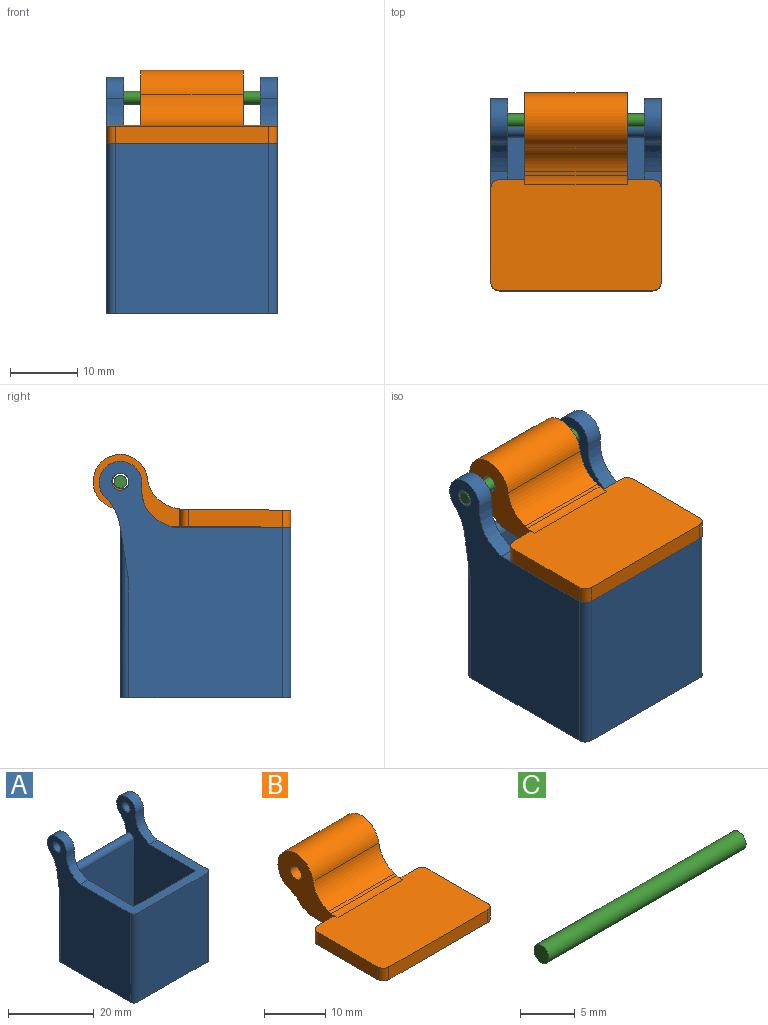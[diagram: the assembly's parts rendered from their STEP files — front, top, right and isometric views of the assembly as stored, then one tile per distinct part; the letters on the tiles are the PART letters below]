
ASSEMBLY  parts=3 mates=2
PART A: 24 faces, bbox 25.4x28.6x35.2 mm
  f0: plane 25.4x17.7mm, normal (0,0,1), area 140.8mm2, adj f1,f2,f4,f6,f9,f10,f13,f15
  f1: plane 35.19x27.31mm, normal (1,0,0), area 634.1mm2, adj f0,f3,f6,f7,f8,f18,f20,f23
  f2: plane 35.19x27.31mm, normal (-1,0,0), area 634.1mm2, adj f0,f3,f10,f11,f12,f17,f19,f22
  f3: plane 25.4x25.4mm, normal (0,0,-1), area 643.8mm2, adj f1,f2,f4,f5,f17,f18,f19,f20
  f4: plane 25.4x22.86mm, normal (0,-1,0), area 580.6mm2, adj f0,f3,f19,f20
  f5: plane 25.4x22.86mm, normal (0,1,0), area 554.8mm2, adj f3,f7,f9,f11,f13,f17,f18,f21
  f6: extruded ~6.66x4.54mm, area 22.4mm2, adj f0,f1,f8,f9
  f7: extruded ~12.99x3.77mm, area 16mm2, adj f1,f5,f8,f9,f18
  f8: cylinder r=3.17mm len=6.35mm, axis (1,0,0), area 30.6mm2, adj f1,f6,f7,f9
  f9: plane 32.65x26.04mm, normal (-1,0,0), area 513.5mm2, adj f0,f5,f6,f7,f8,f14,f15,f16
  f10: extruded ~6.66x4.54mm, area 22.4mm2, adj f0,f2,f12,f13
  f11: extruded ~12.99x3.77mm, area 16mm2, adj f2,f5,f12,f13,f17
  f12: cylinder r=3.17mm len=6.35mm, axis (-1,0,0), area 30.6mm2, adj f2,f10,f11,f13
  f13: plane 32.65x26.04mm, normal (1,0,0), area 513.5mm2, adj f0,f5,f10,f11,f12,f14,f15,f16
  f14: plane 20.32x20.32mm, normal (0,0,1), area 412.9mm2, adj f9,f13,f15,f16
  f15: plane 22.86x20.32mm, normal (0,1,0), area 464.5mm2, adj f0,f9,f13,f14
  f16: plane 21.59x20.32mm, normal (0,-1,0), area 438.7mm2, adj f9,f13,f14,f21
  f17: cylinder r=1.27mm len=25.4mm, axis (0,0,-1), area 44.6mm2, adj f2,f3,f5,f11
  f18: cylinder r=1.27mm len=25.4mm, axis (0,0,1), area 44.6mm2, adj f1,f3,f5,f7
  f19: cylinder r=1.27mm len=25.4mm, axis (0,0,1), area 50.7mm2, adj f0,f2,f3,f4
  f20: cylinder r=1.27mm len=25.4mm, axis (0,0,-1), area 50.7mm2, adj f0,f1,f3,f4
  f21: cylinder r=1.27mm len=20.32mm, axis (-1,0,0), area 81.1mm2, adj f5,f9,f13,f16
  f22: cylinder r=1.27mm len=2.54mm, axis (1,0,0), area 20.3mm2, adj f2,f13
  f23: cylinder r=1.27mm len=2.54mm, axis (1,0,0), area 20.3mm2, adj f1,f9
PART B: 20 faces, bbox 25.4x29.5x10.7 mm
  f0: cylinder r=4.06mm len=15.24mm, axis (1,0,0), area 264.8mm2, adj f1,f2,f11,f14
  f1: plane 13.66x10.67mm, normal (-1,0,0), area 75.9mm2, adj f0,f3,f4,f5,f10,f11,f12,f13
  f2: plane 13.66x10.67mm, normal (1,0,0), area 75.9mm2, adj f0,f3,f4,f9,f10,f11,f12,f13
  f3: plane 15.24x0.53mm, normal (0,-0.27,0.96), area 8.4mm2, adj f1,f2,f11,f12
  f4: plane 25.4x16.51mm, normal (0,0,1), area 407.2mm2, adj f1,f2,f5,f6,f7,f8,f9,f12
  f5: plane 3.81x2.54mm, normal (0,1,0), area 9.7mm2, adj f1,f4,f10,f18
  f6: plane 13.97x2.54mm, normal (-1,0,0), area 35.5mm2, adj f4,f10,f16,f18
  f7: plane 22.86x2.54mm, normal (0,-1,0), area 58.1mm2, adj f4,f10,f15,f16
  f8: plane 13.97x2.54mm, normal (1,0,0), area 35.5mm2, adj f4,f10,f15,f17
  f9: plane 3.81x2.54mm, normal (0,1,0), area 9.7mm2, adj f2,f4,f10,f17
  f10: plane 25.4x21mm, normal (0,0,-1), area 486.4mm2, adj f1,f2,f5,f6,f7,f8,f9,f13
  f11: cylinder r=5.08mm len=15.24mm, axis (1,0,0), area 90.2mm2, adj f0,f1,f2,f3
  f12: cylinder r=5.08mm len=15.24mm, axis (-1,0,0), area 21.5mm2, adj f1,f2,f3,f4
  f13: cylinder r=5.08mm len=15.24mm, axis (1,0,0), area 60.8mm2, adj f1,f2,f10,f14
  f14: cylinder r=5.08mm len=15.24mm, axis (-1,0,0), area 36.8mm2, adj f0,f1,f2,f13
  f15: cylinder r=1.27mm len=2.54mm, axis (0,0,-1), area 5.1mm2, adj f4,f7,f8,f10
  f16: cylinder r=1.27mm len=2.54mm, axis (0,0,1), area 5.1mm2, adj f4,f6,f7,f10
  f17: cylinder r=1.27mm len=2.54mm, axis (0,0,-1), area 5.1mm2, adj f4,f8,f9,f10
  f18: cylinder r=1.27mm len=2.54mm, axis (0,0,-1), area 5.1mm2, adj f4,f5,f6,f10
  f19: cylinder r=1.27mm len=15.24mm, axis (1,0,0), area 121.6mm2, adj f1,f2
PART C: 3 faces, bbox 25.4x1.9x1.9 mm
  f0: cylinder r=0.95mm len=25.4mm, axis (-1,0,0), area 152mm2, adj f1,f2
  f1: plane 1.91x1.91mm, normal (1,0,0), area 2.9mm2, adj f0
  f2: plane 1.91x1.91mm, normal (-1,0,0), area 2.9mm2, adj f0
PLACE A t=(-11.37,4.09,-5.58)mm fixed
PLACE B rot(axis=(1,0,0),0.4deg) t=(-11.37,-8.56,7.18)mm
PLACE C t=(-24.07,4.09,13.87)mm
MATE revolute B.f0 <-> C.f0  axis (1,0,0) through (-11.37,4.09,13.87)mm
MATE revolute C.f0 <-> A.f22  axis (-1,0,0) through (1.33,4.09,13.87)mm
